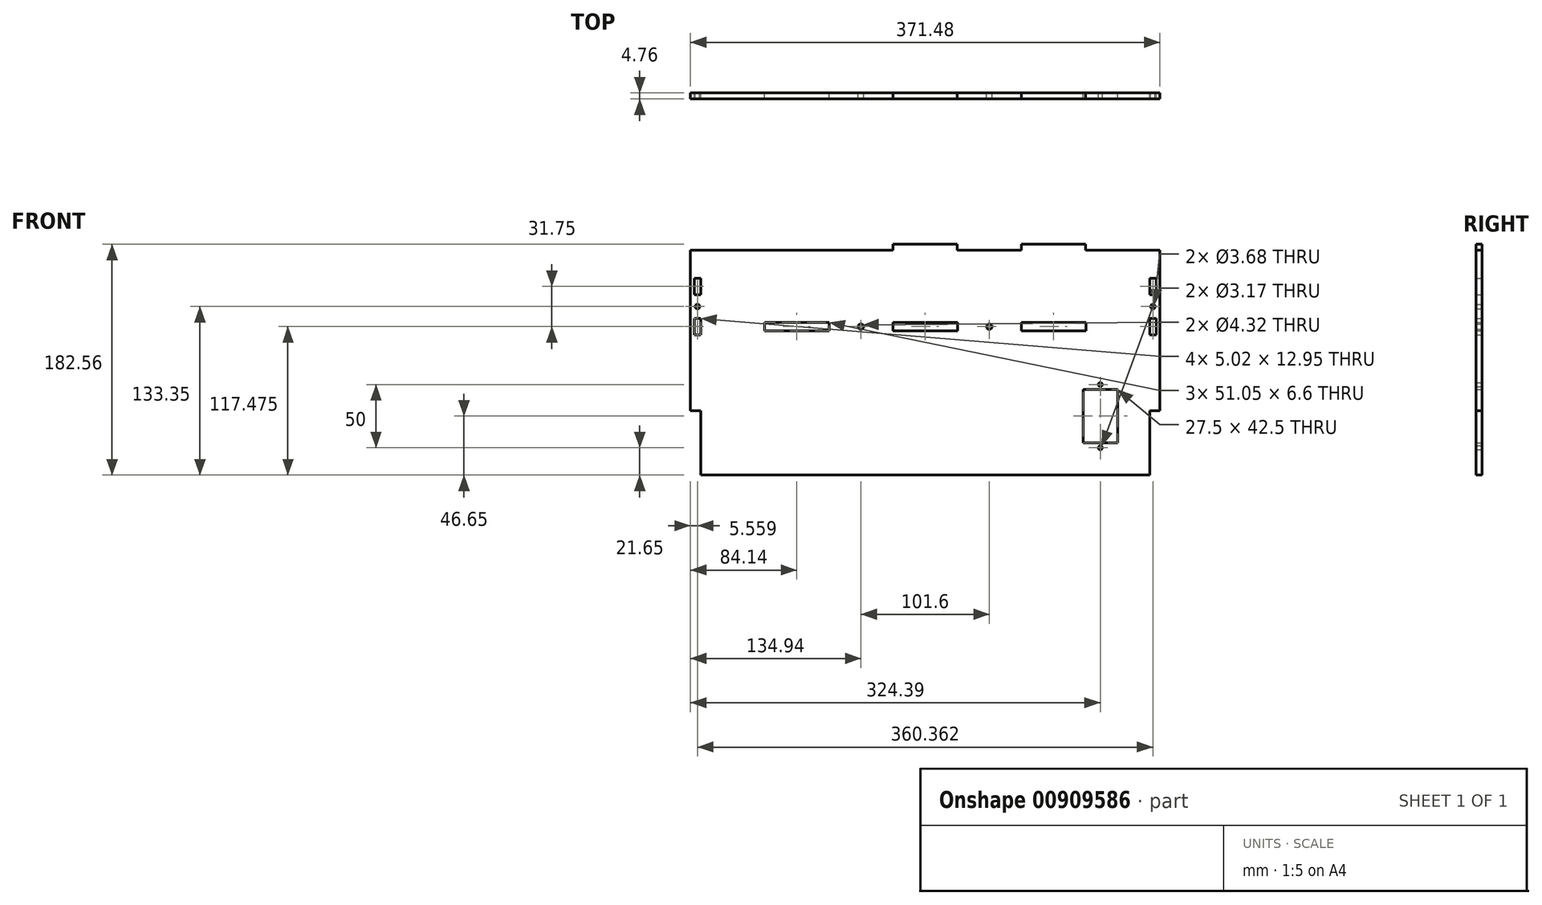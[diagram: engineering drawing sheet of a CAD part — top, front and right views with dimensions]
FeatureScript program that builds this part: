
annotation { "Feature Type Name" : "Feature", "Feature Type Description" : "" }
export const myFeature = defineFeature(function(context is Context, id is Id, definition is map)
    precondition{}
    {
        {
            var Q0;
            Q0=qCreatedBy(makeId("Front.planeOp"),FACE);
            var sketch = newSketch(context, id + "F0", { "sketchPlane" : qUnion([Q0])});
            skLineSegment(sketch, "E0.bottom", {"start": v(-182.56, 88.9) * mm, "end": v(182.56, 88.9) * mm});
            skLineSegment(sketch, "E0.top", {"start": v(-182.56, -88.9) * mm, "end": v(182.56, -88.9) * mm});
            skLineSegment(sketch, "E0.left", {"start": v(-182.56, 88.9) * mm, "end": v(-182.56, -88.9) * mm});
            skLineSegment(sketch, "E0.right", {"start": v(182.56, 88.9) * mm, "end": v(182.56, -88.9) * mm});
            skPoint(sketch, "E0.middle", {"position": v(0, 0) * mm});
            skLineSegment(sketch, "E1.0", {"start": v(-177.8, 88.9) * mm, "end": v(-177.8, -88.9) * mm, "construction": true});
            skLineSegment(sketch, "E2.0", {"start": v(177.8, 88.9) * mm, "end": v(177.8, -88.9) * mm, "construction": true});
            skLineSegment(sketch, "E3.bottom", {"start": v(-127, 31.75) * mm, "end": v(-76.2, 31.75) * mm});
            skLineSegment(sketch, "E3.top", {"start": v(-127, 25.4) * mm, "end": v(-76.2, 25.4) * mm});
            skLineSegment(sketch, "E3.left", {"start": v(-127, 31.75) * mm, "end": v(-127, 25.4) * mm});
            skLineSegment(sketch, "E3.right", {"start": v(-76.2, 31.75) * mm, "end": v(-76.2, 25.4) * mm});
            skLineSegment(sketch, "E4.0", {"start": v(-127.13, 31.88) * mm, "end": v(-76.07, 31.88) * mm});
            skLineSegment(sketch, "E4.1", {"start": v(-127.13, 31.88) * mm, "end": v(-127.13, 25.27) * mm});
            skLineSegment(sketch, "E4.2", {"start": v(-127.13, 25.27) * mm, "end": v(-76.07, 25.27) * mm});
            skLineSegment(sketch, "E4.3", {"start": v(-76.07, 31.88) * mm, "end": v(-76.07, 25.27) * mm});
            skLineSegment(sketch, "E5.1.0.0", {"start": v(-25.53, 31.88) * mm, "end": v(-25.53, 25.27) * mm});
            skLineSegment(sketch, "E5.1.0.1", {"start": v(-25.53, 31.88) * mm, "end": v(25.53, 31.88) * mm});
            skLineSegment(sketch, "E5.1.0.2", {"start": v(-25.53, 25.27) * mm, "end": v(25.53, 25.27) * mm});
            skLineSegment(sketch, "E5.1.0.3", {"start": v(25.4, 31.75) * mm, "end": v(25.4, 25.4) * mm});
            skLineSegment(sketch, "E5.1.0.4", {"start": v(-25.4, 31.75) * mm, "end": v(25.4, 31.75) * mm});
            skLineSegment(sketch, "E5.1.0.5", {"start": v(25.53, 31.88) * mm, "end": v(25.53, 25.27) * mm});
            skLineSegment(sketch, "E5.1.0.6", {"start": v(-25.4, 31.75) * mm, "end": v(-25.4, 25.4) * mm});
            skLineSegment(sketch, "E5.1.0.7", {"start": v(-25.4, 25.4) * mm, "end": v(25.4, 25.4) * mm});
            skLineSegment(sketch, "E5.2.0.0", {"start": v(76.07, 31.88) * mm, "end": v(76.07, 25.27) * mm});
            skLineSegment(sketch, "E5.2.0.1", {"start": v(76.07, 31.88) * mm, "end": v(127.13, 31.88) * mm});
            skLineSegment(sketch, "E5.2.0.2", {"start": v(76.07, 25.27) * mm, "end": v(127.13, 25.27) * mm});
            skLineSegment(sketch, "E5.2.0.3", {"start": v(127, 31.75) * mm, "end": v(127, 25.4) * mm});
            skLineSegment(sketch, "E5.2.0.4", {"start": v(76.2, 31.75) * mm, "end": v(127, 31.75) * mm});
            skLineSegment(sketch, "E5.2.0.5", {"start": v(127.13, 31.88) * mm, "end": v(127.13, 25.27) * mm});
            skLineSegment(sketch, "E5.2.0.6", {"start": v(76.2, 31.75) * mm, "end": v(76.2, 25.4) * mm});
            skLineSegment(sketch, "E5.2.0.7", {"start": v(76.2, 25.4) * mm, "end": v(127, 25.4) * mm});
            skLineSegment(sketch, "E5.direction1", {"start": v(-127, 25.4) * mm, "end": v(-25.4, 25.4) * mm, "construction": true});
            skLineSegment(sketch, "E6.bottom", {"start": v(-182.56, -88.9) * mm, "end": v(-177.8, -88.9) * mm});
            skLineSegment(sketch, "E6.top", {"start": v(-185.74, -38.1) * mm, "end": v(-177.8, -38.1) * mm});
            skLineSegment(sketch, "E6.left", {"start": v(-182.56, -88.9) * mm, "end": v(-182.56, -38.1) * mm});
            skLineSegment(sketch, "E6.right", {"start": v(-177.8, -88.9) * mm, "end": v(-177.8, -38.1) * mm});
            skLineSegment(sketch, "E7", {"start": v(0, 88.9) * mm, "end": v(0, -88.9) * mm, "construction": true});
            skLineSegment(sketch, "E8.MirrorCS", {"start": v(182.56, -88.9) * mm, "end": v(177.8, -88.9) * mm});
            skLineSegment(sketch, "E9.MirrorCS", {"start": v(182.56, -38.1) * mm, "end": v(177.8, -38.1) * mm});
            skLineSegment(sketch, "E10.MirrorCS", {"start": v(182.56, -88.9) * mm, "end": v(182.56, -38.1) * mm});
            skLineSegment(sketch, "E11.MirrorCS", {"start": v(177.8, -88.9) * mm, "end": v(177.8, -38.1) * mm});
            skLineSegment(sketch, "E12.0", {"start": v(-182.69, -89.03) * mm, "end": v(-177.67, -89.03) * mm});
            skLineSegment(sketch, "E12.1", {"start": v(-182.69, -89.03) * mm, "end": v(-182.69, -37.97) * mm});
            skLineSegment(sketch, "E12.2", {"start": v(-182.69, -37.97) * mm, "end": v(-177.67, -37.97) * mm});
            skLineSegment(sketch, "E12.3", {"start": v(-177.67, -89.03) * mm, "end": v(-177.67, -37.97) * mm});
            skLineSegment(sketch, "E13.bottom", {"start": v(-127, 88.9) * mm, "end": v(-76.2, 88.9) * mm});
            skLineSegment(sketch, "E13.top", {"start": v(-127, 93.66) * mm, "end": v(-76.2, 93.66) * mm});
            skLineSegment(sketch, "E13.left", {"start": v(-127, 88.9) * mm, "end": v(-127, 93.66) * mm});
            skLineSegment(sketch, "E13.right", {"start": v(-76.2, 88.9) * mm, "end": v(-76.2, 93.66) * mm});
            skLineSegment(sketch, "E14.1.0.0", {"start": v(-25.4, 93.66) * mm, "end": v(25.4, 93.66) * mm});
            skLineSegment(sketch, "E14.1.0.1", {"start": v(-25.4, 88.9) * mm, "end": v(25.4, 88.9) * mm});
            skLineSegment(sketch, "E14.1.0.2", {"start": v(-25.4, 88.9) * mm, "end": v(-25.4, 93.66) * mm});
            skLineSegment(sketch, "E14.1.0.3", {"start": v(25.4, 88.9) * mm, "end": v(25.4, 93.66) * mm});
            skLineSegment(sketch, "E14.2.0.0", {"start": v(76.2, 93.66) * mm, "end": v(127, 93.66) * mm});
            skLineSegment(sketch, "E14.2.0.1", {"start": v(76.2, 88.9) * mm, "end": v(127, 88.9) * mm});
            skLineSegment(sketch, "E14.2.0.2", {"start": v(76.2, 88.9) * mm, "end": v(76.2, 93.66) * mm});
            skLineSegment(sketch, "E14.2.0.3", {"start": v(127, 88.9) * mm, "end": v(127, 93.66) * mm});
            skLineSegment(sketch, "E14.direction1", {"start": v(-127, 88.9) * mm, "end": v(-25.4, 88.9) * mm, "construction": true});
            skLineSegment(sketch, "E15.MirrorCS", {"start": v(182.69, -89.03) * mm, "end": v(177.67, -89.03) * mm});
            skLineSegment(sketch, "E16.MirrorCS", {"start": v(182.69, -37.97) * mm, "end": v(177.67, -37.97) * mm});
            skLineSegment(sketch, "E17.MirrorCS", {"start": v(182.69, -89.03) * mm, "end": v(182.69, -37.97) * mm});
            skLineSegment(sketch, "E18.MirrorCS", {"start": v(177.67, -89.03) * mm, "end": v(177.67, -37.97) * mm});
            skCircle(sketch, "E19", {"center": v(-180.18, 44.45) * mm, "radius": 1.84 * mm});
            skCircle(sketch, "E20.MirrorC", {"center": v(180.18, 44.45) * mm, "radius": 1.84 * mm});
            skLineSegment(sketch, "E21.0", {"start": v(-185.74, 88.9) * mm, "end": v(-185.74, -38.1) * mm});
            skLineSegment(sketch, "E22", {"start": v(-185.74, 88.9) * mm, "end": v(-182.56, 88.9) * mm});
            skLineSegment(sketch, "E23.MirrorCS", {"start": v(185.74, -38.1) * mm, "end": v(177.8, -38.1) * mm});
            skLineSegment(sketch, "E24.MirrorCS", {"start": v(185.74, 88.9) * mm, "end": v(182.56, 88.9) * mm});
            skLineSegment(sketch, "E25.MirrorCS", {"start": v(185.74, 88.9) * mm, "end": v(185.74, -38.1) * mm});
            skLineSegment(sketch, "E26.bottom", {"start": v(-177.67, 35.05) * mm, "end": v(-182.69, 35.05) * mm});
            skLineSegment(sketch, "E26.top", {"start": v(-177.67, 22.1) * mm, "end": v(-182.69, 22.1) * mm});
            skLineSegment(sketch, "E26.left", {"start": v(-177.67, 35.05) * mm, "end": v(-177.67, 22.1) * mm});
            skLineSegment(sketch, "E26.right", {"start": v(-182.69, 35.05) * mm, "end": v(-182.69, 22.1) * mm});
            skPoint(sketch, "E26.middle", {"position": v(-180.18, 28.58) * mm});
            skPoint(sketch, "E26.middle.positionSnap0", {"position": v(-180.18, -37.97) * mm});
            skPoint(sketch, "E26.centerSnap0", {"position": v(-180.18, -37.97) * mm});
            skLineSegment(sketch, "E27", {"start": v(-185.74, 44.45) * mm, "end": v(-177.8, 44.45) * mm, "construction": true});
            skLineSegment(sketch, "E28.MirrorCS", {"start": v(-177.67, 53.85) * mm, "end": v(-182.69, 53.85) * mm});
            skPoint(sketch, "E29.MirrorP", {"position": v(-180.18, 60.33) * mm});
            skLineSegment(sketch, "E30.MirrorCS", {"start": v(-177.67, 66.8) * mm, "end": v(-182.69, 66.8) * mm});
            skLineSegment(sketch, "E31.MirrorCS", {"start": v(-182.69, 53.85) * mm, "end": v(-182.69, 66.8) * mm});
            skLineSegment(sketch, "E32.MirrorCS", {"start": v(-177.67, 53.85) * mm, "end": v(-177.67, 66.8) * mm});
            skLineSegment(sketch, "E33.MirrorCS", {"start": v(182.69, 53.85) * mm, "end": v(182.69, 66.8) * mm});
            skLineSegment(sketch, "E34.MirrorCS", {"start": v(177.67, 66.8) * mm, "end": v(182.69, 66.8) * mm});
            skLineSegment(sketch, "E35.MirrorCS", {"start": v(177.67, 53.85) * mm, "end": v(177.67, 66.8) * mm});
            skLineSegment(sketch, "E36.MirrorCS", {"start": v(177.67, 53.85) * mm, "end": v(182.69, 53.85) * mm});
            skPoint(sketch, "E37.MirrorP", {"position": v(180.18, 60.33) * mm});
            skLineSegment(sketch, "E38.MirrorCS", {"start": v(177.67, 35.05) * mm, "end": v(182.69, 35.05) * mm});
            skLineSegment(sketch, "E39.MirrorCS", {"start": v(182.69, 35.05) * mm, "end": v(182.69, 22.1) * mm});
            skLineSegment(sketch, "E40.MirrorCS", {"start": v(177.67, 35.05) * mm, "end": v(177.67, 22.1) * mm});
            skLineSegment(sketch, "E41.MirrorCS", {"start": v(177.67, 22.1) * mm, "end": v(182.69, 22.1) * mm});
            skPoint(sketch, "E42.MirrorP", {"position": v(180.18, 28.57) * mm});
            skLineSegment(sketch, "E43.bottom", {"start": v(124.9, -21) * mm, "end": v(152.4, -21) * mm});
            skLineSegment(sketch, "E43.top", {"start": v(124.9, -63.5) * mm, "end": v(152.4, -63.5) * mm});
            skLineSegment(sketch, "E43.left", {"start": v(124.9, -21) * mm, "end": v(124.9, -63.5) * mm});
            skLineSegment(sketch, "E43.right", {"start": v(152.4, -21) * mm, "end": v(152.4, -63.5) * mm});
            skCircle(sketch, "E44", {"center": v(138.65, -17.25) * mm, "radius": 1.59 * mm});
            skPoint(sketch, "E44.centerSnap0", {"position": v(138.65, -21) * mm});
            skLineSegment(sketch, "E45", {"start": v(124.9, -42.25) * mm, "end": v(152.4, -42.25) * mm, "construction": true});
            skCircle(sketch, "E46.MirrorC", {"center": v(138.65, -67.25) * mm, "radius": 1.59 * mm});
            skLineSegment(sketch, "E47", {"start": v(-127, 28.58) * mm, "end": v(-177.8, 28.58) * mm, "construction": true});
            skLineSegment(sketch, "E48", {"start": v(-76.2, 28.58) * mm, "end": v(-25.4, 28.58) * mm, "construction": true});
            skLineSegment(sketch, "E49", {"start": v(25.4, 28.58) * mm, "end": v(76.2, 28.58) * mm, "construction": true});
            skLineSegment(sketch, "E50", {"start": v(127, 28.58) * mm, "end": v(177.8, 28.58) * mm, "construction": true});
            skCircle(sketch, "E51", {"center": v(-152.4, 28.58) * mm, "radius": 1.59 * mm, "construction": true});
            skCircle(sketch, "E52", {"center": v(-50.8, 28.58) * mm, "radius": 1.59 * mm, "construction": true});
            skCircle(sketch, "E53", {"center": v(50.8, 28.58) * mm, "radius": 1.59 * mm, "construction": true});
            skCircle(sketch, "E54", {"center": v(152.4, 28.58) * mm, "radius": 1.59 * mm, "construction": true});
            skSolve(sketch);
        }
        {
            var Q0;
            Q0=makeQuery(id+"F0.imprint","IMPRINT",FACE,{"disambiguationData":[TD([[makeQuery(id+"F0.imprint","IMPRINT",EDGE,{"derivedFrom":sQuery(id+"F0.wireOp",EDGE,"E0.bottom")}),-1.0]])]});
            var Q1;
            Q1=makeQuery(id+"F0.imprint","IMPRINT",FACE,{"disambiguationData":[TD([[makeQuery(id+"F0.imprint","IMPRINT",EDGE,{"derivedFrom":sQuery(id+"F0.wireOp",EDGE,"E13.bottom")}),1.0]])]});
            var Q2;
            Q2=makeQuery(id+"F0.imprint","IMPRINT",FACE,{"disambiguationData":[TD([[makeQuery(id+"F0.imprint","IMPRINT",EDGE,{"derivedFrom":sQuery(id+"F0.wireOp",EDGE,"E14.1.0.0")}),-1.0]])]});
            var Q3;
            Q3=makeQuery(id+"F0.imprint","IMPRINT",FACE,{"disambiguationData":[TD([[makeQuery(id+"F0.imprint","IMPRINT",EDGE,{"derivedFrom":sQuery(id+"F0.wireOp",EDGE,"E14.2.0.0")}),-1.0]])]});
            var Q4;
            {var subQ9=sQuery(id+"F0.wireOp",EDGE,"E22");Q4=makeQuery(id+"F0.imprint","IMPRINT",FACE,{"disambiguationData":[TD([[makeQuery(id+"F0.imprint","IMPRINT",EDGE,{"derivedFrom":subQ9}),-1.0]])]});}
            var Q5;
            {var subQ6=sQuery(id+"F0.wireOp",EDGE,"E24.MirrorCS");Q5=makeQuery(id+"F0.imprint","IMPRINT",FACE,{"disambiguationData":[TD([[makeQuery(id+"F0.imprint","IMPRINT",EDGE,{"derivedFrom":subQ6}),1.0]])]});}
            extrude(context, id + "F1", {"entities" : qUnion([Q0, Q1, Q2, Q3, Q4, Q5]), "depth" : 4.76 * mm, "offsetDistance" : 25.4 * mm});
        }
        {
            var Q0;
            Q0=sQuery(id+"F0.wireOp",VERTEX,"E52.center");
            var Q1;
            Q1=sQuery(id+"F0.wireOp",VERTEX,"E53.center");
            var Q2;
            Q2=makeQuery(id+"F1.opExtrude","SWEPT_BODY",BODY,{"disambiguationData":[OSD([sQuery(id+"F0.wireOp",EDGE,"E0.bottom"),sQuery(id+"F0.wireOp",EDGE,"E0.top"),sQuery(id+"F0.wireOp",EDGE,"E4.0"),sQuery(id+"F0.wireOp",EDGE,"E4.1"),sQuery(id+"F0.wireOp",EDGE,"E4.2"),sQuery(id+"F0.wireOp",EDGE,"E4.3"),sQuery(id+"F0.wireOp",EDGE,"E5.1.0.0"),sQuery(id+"F0.wireOp",EDGE,"E5.1.0.1"),sQuery(id+"F0.wireOp",EDGE,"E5.1.0.2"),sQuery(id+"F0.wireOp",EDGE,"E5.1.0.5"),sQuery(id+"F0.wireOp",EDGE,"E5.2.0.0"),sQuery(id+"F0.wireOp",EDGE,"E5.2.0.1"),sQuery(id+"F0.wireOp",EDGE,"E5.2.0.2"),sQuery(id+"F0.wireOp",EDGE,"E5.2.0.5"),sQuery(id+"F0.wireOp",EDGE,"E6.top"),sQuery(id+"F0.wireOp",EDGE,"E12.1"),sQuery(id+"F0.wireOp",EDGE,"E12.2"),sQuery(id+"F0.wireOp",EDGE,"E12.3"),sQuery(id+"F0.wireOp",EDGE,"E13.top"),sQuery(id+"F0.wireOp",EDGE,"E13.left"),sQuery(id+"F0.wireOp",EDGE,"E13.right"),sQuery(id+"F0.wireOp",EDGE,"E14.1.0.0"),sQuery(id+"F0.wireOp",EDGE,"E14.1.0.2"),sQuery(id+"F0.wireOp",EDGE,"E14.1.0.3"),sQuery(id+"F0.wireOp",EDGE,"E14.2.0.0"),sQuery(id+"F0.wireOp",EDGE,"E14.2.0.2"),sQuery(id+"F0.wireOp",EDGE,"E14.2.0.3"),sQuery(id+"F0.wireOp",EDGE,"E17.MirrorCS"),sQuery(id+"F0.wireOp",EDGE,"E18.MirrorCS"),sQuery(id+"F0.wireOp",EDGE,"E19"),sQuery(id+"F0.wireOp",EDGE,"E21.0"),sQuery(id+"F0.wireOp",EDGE,"E22"),sQuery(id+"F0.wireOp",EDGE,"E23.MirrorCS"),sQuery(id+"F0.wireOp",EDGE,"E24.MirrorCS"),sQuery(id+"F0.wireOp",EDGE,"E16.MirrorCS"),sQuery(id+"F0.wireOp",EDGE,"E20.MirrorC"),sQuery(id+"F0.wireOp",EDGE,"E25.MirrorCS"),sQuery(id+"F0.wireOp",EDGE,"E26.bottom"),sQuery(id+"F0.wireOp",EDGE,"E26.top"),sQuery(id+"F0.wireOp",EDGE,"E26.left"),sQuery(id+"F0.wireOp",EDGE,"E26.right"),sQuery(id+"F0.wireOp",EDGE,"E28.MirrorCS"),sQuery(id+"F0.wireOp",EDGE,"E30.MirrorCS"),sQuery(id+"F0.wireOp",EDGE,"E31.MirrorCS"),sQuery(id+"F0.wireOp",EDGE,"E32.MirrorCS"),sQuery(id+"F0.wireOp",EDGE,"E33.MirrorCS"),sQuery(id+"F0.wireOp",EDGE,"E34.MirrorCS"),sQuery(id+"F0.wireOp",EDGE,"E35.MirrorCS"),sQuery(id+"F0.wireOp",EDGE,"E36.MirrorCS"),sQuery(id+"F0.wireOp",EDGE,"E38.MirrorCS"),sQuery(id+"F0.wireOp",EDGE,"E39.MirrorCS"),sQuery(id+"F0.wireOp",EDGE,"E40.MirrorCS"),sQuery(id+"F0.wireOp",EDGE,"E41.MirrorCS"),sQuery(id+"F0.wireOp",EDGE,"E43.bottom"),sQuery(id+"F0.wireOp",EDGE,"E43.top"),sQuery(id+"F0.wireOp",EDGE,"E43.left"),sQuery(id+"F0.wireOp",EDGE,"E43.right"),sQuery(id+"F0.wireOp",EDGE,"E44"),sQuery(id+"F0.wireOp",EDGE,"E46.MirrorC")])]});
            hole(context, id + "F2", {"style" : HoleStyle.SIMPLE, "endStyle" : HoleEndStyle.BLIND, "oppositeDirection" : true, "standardTappedOrClearance" : lookupTablePath({ "fit" : "Normal (ASME)", "standard" : "ANSI", "size" : "#6", "type" : "Clearance" }), "standardBlindInLast" : lookupTablePath({ "fit" : "Normal", "standard" : "ANSI", "size" : "#6", "type" : "Clearance" }), "holeDiameter" : 4.32 * mm, "majorDiameter" : 6.35 * mm, "holeDepth" : 11.9 * mm, "isTappedThrough" : true, "tappedDepth" : 9.52 * mm, "tapClearance" : 3, "locations" : qUnion([Q0, Q1]), "scope" : qUnion([Q2])});
        }
    });
